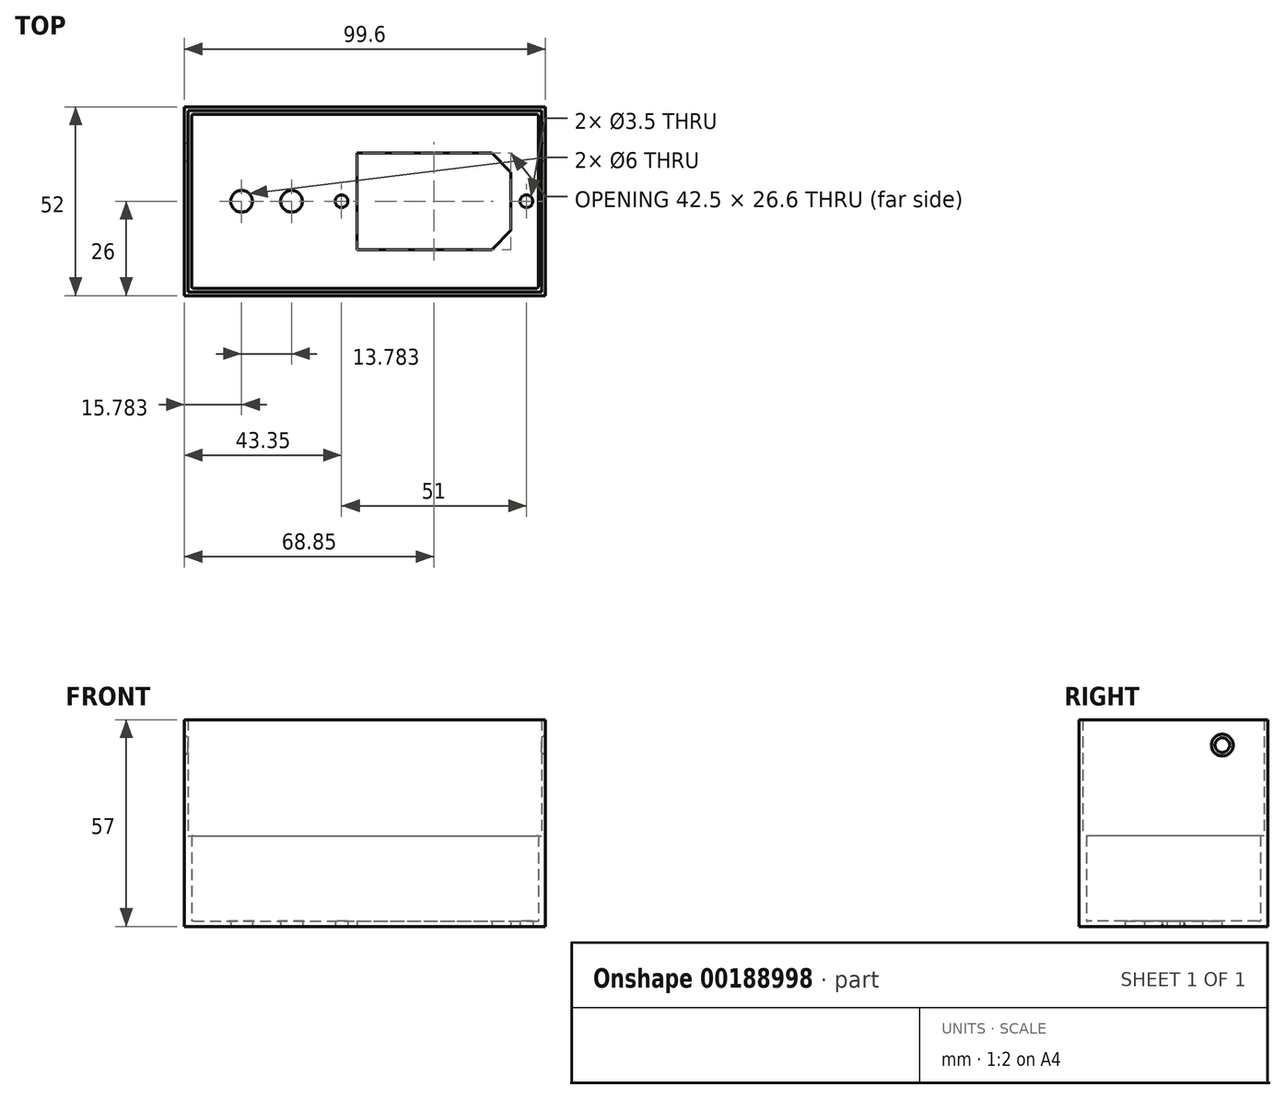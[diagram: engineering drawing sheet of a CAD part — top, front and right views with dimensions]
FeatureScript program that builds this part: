
annotation { "Feature Type Name" : "Feature", "Feature Type Description" : "" }
export const myFeature = defineFeature(function(context is Context, id is Id, definition is map)
    precondition{}
    {
        {
            assignVariable(context, id + "F0", {"name" : "wall_thickness", "anyValue" : 1});
        }
        {
            var Q0;
            Q0=qCreatedBy(makeId("Top.planeOp"),FACE);
            var sketch = newSketch(context, id + "F1", { "sketchPlane" : qUnion([Q0])});
            skLineSegment(sketch, "E0.bottom", {"start": v(-48.8, 25) * mm, "end": v(48.8, 25) * mm});
            skLineSegment(sketch, "E0.top", {"start": v(-48.8, -25) * mm, "end": v(48.8, -25) * mm});
            skLineSegment(sketch, "E0.left", {"start": v(-48.8, 25) * mm, "end": v(-48.8, -25) * mm});
            skLineSegment(sketch, "E0.right", {"start": v(48.8, 25) * mm, "end": v(48.8, -25) * mm});
            skLineSegment(sketch, "E1.bottom", {"start": v(-49.8, 26) * mm, "end": v(49.8, 26) * mm});
            skLineSegment(sketch, "E1.top", {"start": v(-49.8, -26) * mm, "end": v(49.8, -26) * mm});
            skLineSegment(sketch, "E1.left", {"start": v(-49.8, 26) * mm, "end": v(-49.8, -26) * mm});
            skLineSegment(sketch, "E1.right", {"start": v(49.8, 26) * mm, "end": v(49.8, -26) * mm});
            skLineSegment(sketch, "E2", {"start": v(-2.2, 13.3) * mm, "end": v(35, 13.3) * mm});
            skLineSegment(sketch, "E3", {"start": v(35, 13.3) * mm, "end": v(40.3, 8) * mm});
            skLineSegment(sketch, "E4", {"start": v(40.3, 8) * mm, "end": v(40.3, -8) * mm});
            skLineSegment(sketch, "E5", {"start": v(40.3, -8) * mm, "end": v(35, -13.3) * mm});
            skLineSegment(sketch, "E6", {"start": v(35, -13.3) * mm, "end": v(-2.2, -13.3) * mm});
            skLineSegment(sketch, "E7", {"start": v(-2.2, -13.3) * mm, "end": v(-2.2, 13.3) * mm});
            skCircle(sketch, "E8", {"center": v(-6.45, 0) * mm, "radius": 1.75 * mm});
            skCircle(sketch, "E9", {"center": v(44.55, 0) * mm, "radius": 1.75 * mm});
            skLineSegment(sketch, "E10", {"start": v(-6.45, 0) * mm, "end": v(-2.2, 0) * mm, "construction": true});
            skLineSegment(sketch, "E11", {"start": v(40.3, 0) * mm, "end": v(44.55, 0) * mm, "construction": true});
            skLineSegment(sketch, "E12", {"start": v(44.55, 0) * mm, "end": v(48.8, 0) * mm, "construction": true});
            skLineSegment(sketch, "E13.bottom", {"start": v(-47.8, 24) * mm, "end": v(47.8, 24) * mm});
            skLineSegment(sketch, "E13.top", {"start": v(-47.8, -24) * mm, "end": v(47.8, -24) * mm});
            skLineSegment(sketch, "E13.left", {"start": v(-47.8, 24) * mm, "end": v(-47.8, -24) * mm});
            skLineSegment(sketch, "E13.right", {"start": v(47.8, 24) * mm, "end": v(47.8, -24) * mm});
            skCircle(sketch, "E14", {"center": v(-34.02, 0) * mm, "radius": 3 * mm});
            skCircle(sketch, "E15", {"center": v(-20.23, 0) * mm, "radius": 3 * mm});
            skLineSegment(sketch, "E16", {"start": v(-47.8, 0) * mm, "end": v(-34.02, 0) * mm, "construction": true});
            skLineSegment(sketch, "E17", {"start": v(-6.45, 0) * mm, "end": v(-20.23, 0) * mm, "construction": true});
            skLineSegment(sketch, "E18", {"start": v(-20.23, 0) * mm, "end": v(-34.02, 0) * mm, "construction": true});
            skSolve(sketch);
        }
        {
            var Q0;
            Q0=makeQuery(id+"F1.imprint","IMPRINT",FACE,{"disambiguationData":[TD([[makeQuery(id+"F1.imprint","IMPRINT",EDGE,{"derivedFrom":sQuery(id+"F1.wireOp",EDGE,"E2")}),1.0]])]});
            extrude(context, id + "F2", {"entities" : qUnion([Q0]), "depth" : 1.5 * mm});
        }
        {
            var Q0;
            Q0=makeQuery(id+"F1.imprint","IMPRINT",FACE,{"disambiguationData":[TD([[makeQuery(id+"F1.imprint","IMPRINT",EDGE,{"derivedFrom":sQuery(id+"F1.wireOp",EDGE,"E0.bottom")}),-1.0]])]});
            extrude(context, id + "F3", {"entities" : qUnion([Q0]), "operationType" : NewBodyOperationType.ADD, "depth" : 25 * mm});
        }
        {
            var Q0;
            Q0=makeQuery(id+"F1.imprint","IMPRINT",FACE,{"disambiguationData":[TD([[makeQuery(id+"F1.imprint","IMPRINT",EDGE,{"derivedFrom":sQuery(id+"F1.wireOp",EDGE,"E0.bottom")}),1.0]])]});
            extrude(context, id + "F4", {"entities" : qUnion([Q0]), "operationType" : NewBodyOperationType.ADD, "depth" : (25 + 32) * mm});
        }
        {
            var Q0;
            Q0=qCreatedBy(makeId("Right.planeOp"),FACE);
            var sketch = newSketch(context, id + "F5", { "sketchPlane" : qUnion([Q0])});
            skCircle(sketch, "E19", {"center": v(13.5, 50) * mm, "radius": 2 * mm});
            skSolve(sketch);
        }
        {
            var Q0;
            Q0=makeQuery(id+"F5.imprint","IMPRINT",FACE,{"disambiguationData":[TD([[makeQuery(id+"F5.imprint","IMPRINT",EDGE,{"derivedFrom":sQuery(id+"F5.wireOp",EDGE,"E19")}),1.0]])]});
            extrude(context, id + "F6", {"entities" : qUnion([Q0]), "operationType" : NewBodyOperationType.REMOVE, "endBound" : BoundingType.THROUGH_ALL, "oppositeDirection" : true, "depth" : 25 * mm, "hasSecondDirection" : true, "secondDirectionBound" : SecondDirectionBoundingType.THROUGH_ALL, "secondDirectionOppositeDirection" : false, "secondDirectionDepth" : 25 * mm});
        }
        {
            var Q0;
            Q0=makeQuery(id+"F6.boolean.opBoolean","INTERSECT",EDGE,{"derivedFrom":[makeQuery(id+"F4.opExtrude","SWEPT_FACE",FACE,{"disambiguationData":[OSD([sQuery(id+"F1.wireOp",EDGE,"E1.right")])]}),makeQuery(id+"F6.opExtrude","SWEPT_FACE",FACE,{"disambiguationData":[OSD([sQuery(id+"F5.wireOp",EDGE,"E19")])]})]});
            var Q1;
            Q1=makeQuery(id+"F6.boolean.opBoolean","INTERSECT",EDGE,{"derivedFrom":[makeQuery(id+"F4.opExtrude","SWEPT_FACE",FACE,{"disambiguationData":[OSD([sQuery(id+"F1.wireOp",EDGE,"E1.left")])]}),makeQuery(id+"F6.opExtrude","SWEPT_FACE",FACE,{"disambiguationData":[OSD([sQuery(id+"F5.wireOp",EDGE,"E19")])]})]});
            chamfer(context, id + "F7", {"entities" : qUnion([Q0, Q1]), "width" : (getVariable(context, 'wall_thickness')) * mm, "tangentPropagation" : true});
        }
        {
            var Q0;
            Q0=makeQuery(id+"F2.opExtrude","SWEPT_FACE",FACE,{"disambiguationData":[OSD([sQuery(id+"F1.wireOp",EDGE,"E15")])]});
            var Q1;
            Q1=makeQuery(id+"F2.opExtrude","SWEPT_FACE",FACE,{"disambiguationData":[OSD([sQuery(id+"F1.wireOp",EDGE,"E14")])]});
            var Q2;
            Q2=makeQuery(id+"F2.opExtrude","CAP_EDGE",EDGE,{"disambiguationData":[OSD([sQuery(id+"F1.wireOp",EDGE,"E13.left")])],"isStart":false});
            var Q3;
            Q3=makeQuery(id+"F2.opExtrude","CAP_EDGE",EDGE,{"disambiguationData":[OSD([sQuery(id+"F1.wireOp",EDGE,"E13.bottom")])],"isStart":false});
            var Q4;
            Q4=makeQuery(id+"F2.opExtrude","CAP_EDGE",EDGE,{"disambiguationData":[OSD([sQuery(id+"F1.wireOp",EDGE,"E13.right")])],"isStart":false});
            var Q5;
            Q5=makeQuery(id+"F3.opExtrude","SWEPT_EDGE",EDGE,{"disambiguationData":[OSD([sQuery(id+"F1.wireOp",EDGE,"E13.bottom"),sQuery(id+"F1.wireOp",EDGE,"E13.right")])]});
            var Q6;
            Q6=makeQuery(id+"F3.opExtrude","SWEPT_EDGE",EDGE,{"disambiguationData":[OSD([sQuery(id+"F1.wireOp",EDGE,"E13.bottom"),sQuery(id+"F1.wireOp",EDGE,"E13.left")])]});
            var Q7;
            Q7=makeQuery(id+"F3.opExtrude","SWEPT_EDGE",EDGE,{"disambiguationData":[OSD([sQuery(id+"F1.wireOp",EDGE,"E13.top"),sQuery(id+"F1.wireOp",EDGE,"E13.left")])]});
            var Q8;
            Q8=makeQuery(id+"F2.opExtrude","CAP_EDGE",EDGE,{"disambiguationData":[OSD([sQuery(id+"F1.wireOp",EDGE,"E13.top")])],"isStart":false});
            var Q9;
            Q9=makeQuery(id+"F3.opExtrude","SWEPT_EDGE",EDGE,{"disambiguationData":[OSD([sQuery(id+"F1.wireOp",EDGE,"E13.top"),sQuery(id+"F1.wireOp",EDGE,"E13.right")])]});
            fillet(context, id + "F8", {"entities" : qUnion([Q0, Q1, Q2, Q3, Q4, Q5, Q6, Q7, Q8, Q9]), "radius" : 0.5 * mm, "tangentPropagation" : true, "allowEdgeOverflow" : false});
        }
    });
